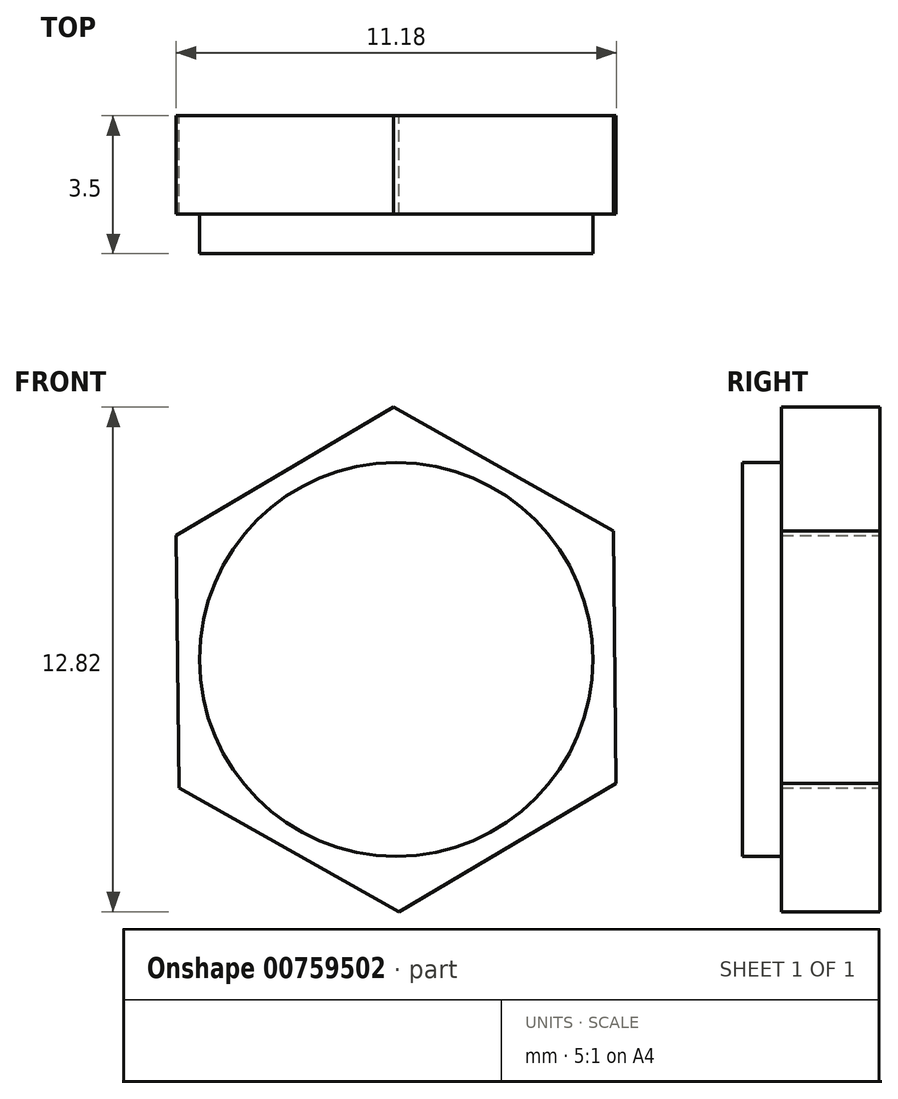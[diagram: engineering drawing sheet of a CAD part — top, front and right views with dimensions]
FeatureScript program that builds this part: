
annotation { "Feature Type Name" : "Feature", "Feature Type Description" : "" }
export const myFeature = defineFeature(function(context is Context, id is Id, definition is map)
    precondition{}
    {
        {
            var Q0;
            Q0=qCreatedBy(makeId("Front.planeOp"),FACE);
            var sketch = newSketch(context, id + "F0", { "sketchPlane" : qUnion([Q0])});
            skCircle(sketch, "E0.cCircle", {"center": v(0, 0) * mm, "radius": 5.55 * mm, "construction": true});
            skLineSegment(sketch, "E0.0", {"start": v(-5.59, 3.15) * mm, "end": v(-0.07, 6.41) * mm});
            skLineSegment(sketch, "E0.1", {"start": v(-0.07, 6.41) * mm, "end": v(5.52, 3.27) * mm});
            skLineSegment(sketch, "E0.2", {"start": v(5.52, 3.27) * mm, "end": v(5.59, -3.15) * mm});
            skLineSegment(sketch, "E0.3", {"start": v(5.59, -3.15) * mm, "end": v(0.07, -6.41) * mm});
            skLineSegment(sketch, "E0.4", {"start": v(0.07, -6.41) * mm, "end": v(-5.52, -3.27) * mm});
            skLineSegment(sketch, "E0.5", {"start": v(-5.52, -3.27) * mm, "end": v(-5.59, 3.15) * mm});
            skPoint(sketch, "E0.0.midPoint", {"position": v(-2.83, 4.78) * mm});
            skSolve(sketch);
        }
        {
            var Q0;
            Q0=makeQuery(id+"F0.imprint","IMPRINT",FACE,{"disambiguationData":[TD([[makeQuery(id+"F0.imprint","IMPRINT",EDGE,{"derivedFrom":sQuery(id+"F0.wireOp",EDGE,"E0.0")}),-1.0]])]});
            extrude(context, id + "F1", {"entities" : qUnion([Q0]), "depth" : 2.5 * mm, "offsetDistance" : 25 * mm});
        }
        {
            var Q0;
            Q0=qCreatedBy(makeId("Front.planeOp"),FACE);
            var sketch = newSketch(context, id + "F2", { "sketchPlane" : qUnion([Q0])});
            skCircle(sketch, "E1", {"center": v(0, 0) * mm, "radius": 5 * mm});
            skSolve(sketch);
        }
        {
            var Q0;
            Q0 = qSketchRegion(id + "F2", true);
            extrude(context, id + "F3", {"entities" : qUnion([Q0]), "operationType" : NewBodyOperationType.ADD, "depth" : 3.5 * mm, "offsetDistance" : 25 * mm});
        }
    });
